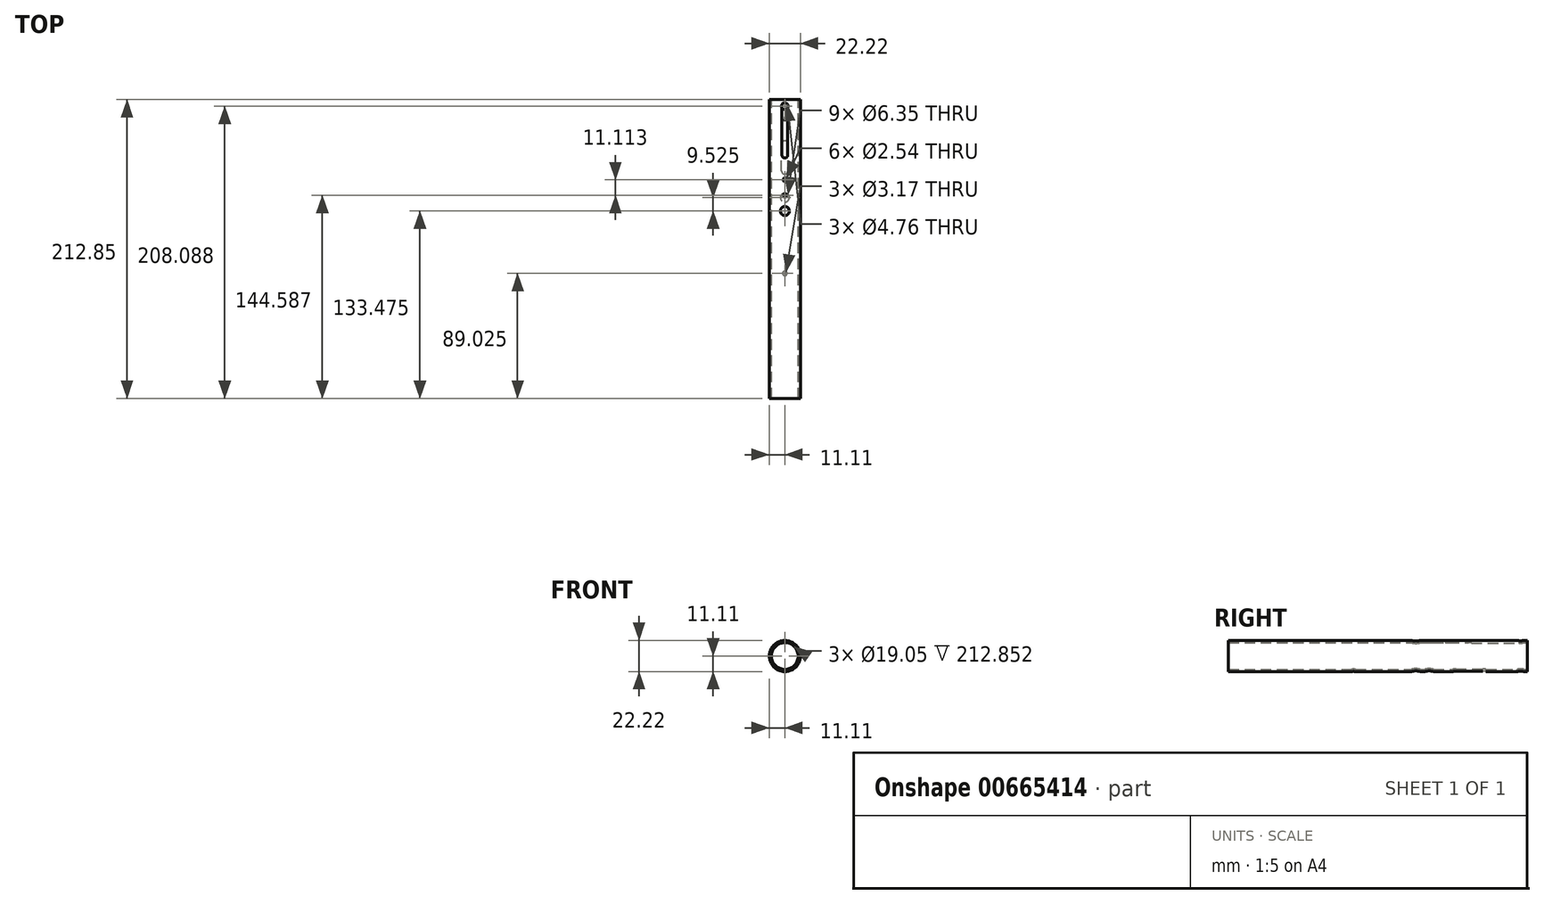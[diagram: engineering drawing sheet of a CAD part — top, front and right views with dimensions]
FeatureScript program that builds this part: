
annotation { "Feature Type Name" : "Feature", "Feature Type Description" : "" }
export const myFeature = defineFeature(function(context is Context, id is Id, definition is map)
    precondition{}
    {
        {
            var Q0;
            Q0=qCreatedBy(makeId("Front.planeOp"),FACE);
            var sketch = newSketch(context, id + "F0", { "sketchPlane" : qUnion([Q0])});
            skCircle(sketch, "E0", {"center": v(0, 0) * mm, "radius": 11.11 * mm});
            skCircle(sketch, "E1", {"center": v(0, 0) * mm, "radius": 9.53 * mm});
            skSolve(sketch);
        }
        {
            var Q0;
            Q0=makeQuery(id+"F0.imprint","IMPRINT",FACE,{"disambiguationData":[TD([[makeQuery(id+"F0.imprint","IMPRINT",EDGE,{"derivedFrom":sQuery(id+"F0.wireOp",EDGE,"E0")}),1.0]])]});
            extrude(context, id + "F1", {"entities" : qUnion([Q0]), "depth" : 212.85 * mm, "offsetDistance" : 25.4 * mm});
        }
        {
            var Q0;
            Q0=qCreatedBy(makeId("Top.planeOp"),FACE);
            var sketch = newSketch(context, id + "F2", { "sketchPlane" : qUnion([Q0])});
            skCircle(sketch, "E2", {"center": v(0, -4.76) * mm, "radius": 2.38 * mm});
            skLineSegment(sketch, "E3", {"start": v(2.38, -50.8) * mm, "end": v(2.38, -31.75) * mm});
            skLineSegment(sketch, "E4", {"start": v(-2.38, -50.8) * mm, "end": v(-2.38, -31.75) * mm});
            skArc(sketch, "E5", {"start": v(2.38, -31.75) * mm, "mid": v(0, -29.37) * mm, "end": v(-2.38, -31.75) * mm});
            skArc(sketch, "E6", {"start": v(-2.38, -50.8) * mm, "mid": v(0, -53.18) * mm, "end": v(2.38, -50.8) * mm});
            skCircle(sketch, "E7", {"center": v(0, -69.85) * mm, "radius": 3.18 * mm});
            skCircle(sketch, "E8", {"center": v(0, -79.38) * mm, "radius": 3.18 * mm});
            skCircle(sketch, "E9", {"center": v(0, -123.83) * mm, "radius": 1.59 * mm});
            skSolve(sketch);
        }
        {
            var Q0;
            Q0 = qSketchRegion(id + "F2", true);
            extrude(context, id + "F3", {"entities" : qUnion([Q0]), "operationType" : NewBodyOperationType.REMOVE, "oppositeDirection" : true, "depth" : 25.4 * mm, "offsetDistance" : 25.4 * mm});
        }
        {
            var Q0;
            Q0=qCreatedBy(makeId("Top.planeOp"),FACE);
            var sketch = newSketch(context, id + "F4", { "sketchPlane" : qUnion([Q0])});
            skCircle(sketch, "E10", {"center": v(0, -4.76) * mm, "radius": 2.38 * mm});
            skLineSegment(sketch, "E11", {"start": v(0, -39.69) * mm, "end": v(2.03, -39.69) * mm});
            skLineSegment(sketch, "E12", {"start": v(0, -39.69) * mm, "end": v(-2.03, -39.69) * mm});
            skArc(sketch, "E13", {"start": v(-2.03, -39.69) * mm, "mid": v(0, -41.7) * mm, "end": v(2.03, -39.69) * mm});
            skLineSegment(sketch, "E14", {"start": v(2.03, -39.69) * mm, "end": v(2.03, -6) * mm});
            skLineSegment(sketch, "E15", {"start": v(-2.03, -39.69) * mm, "end": v(-2.03, -6) * mm});
            skCircle(sketch, "E16", {"center": v(0, -57.15) * mm, "radius": 1.27 * mm});
            skCircle(sketch, "E17", {"center": v(0, -68.26) * mm, "radius": 1.27 * mm});
            skCircle(sketch, "E18", {"center": v(0, -79.38) * mm, "radius": 3.18 * mm});
            skSolve(sketch);
        }
        {
            var Q0;
            Q0 = qSketchRegion(id + "F4", true);
            extrude(context, id + "F5", {"entities" : qUnion([Q0]), "operationType" : NewBodyOperationType.REMOVE, "depth" : 25.4 * mm, "offsetDistance" : 25.4 * mm});
        }
    });
